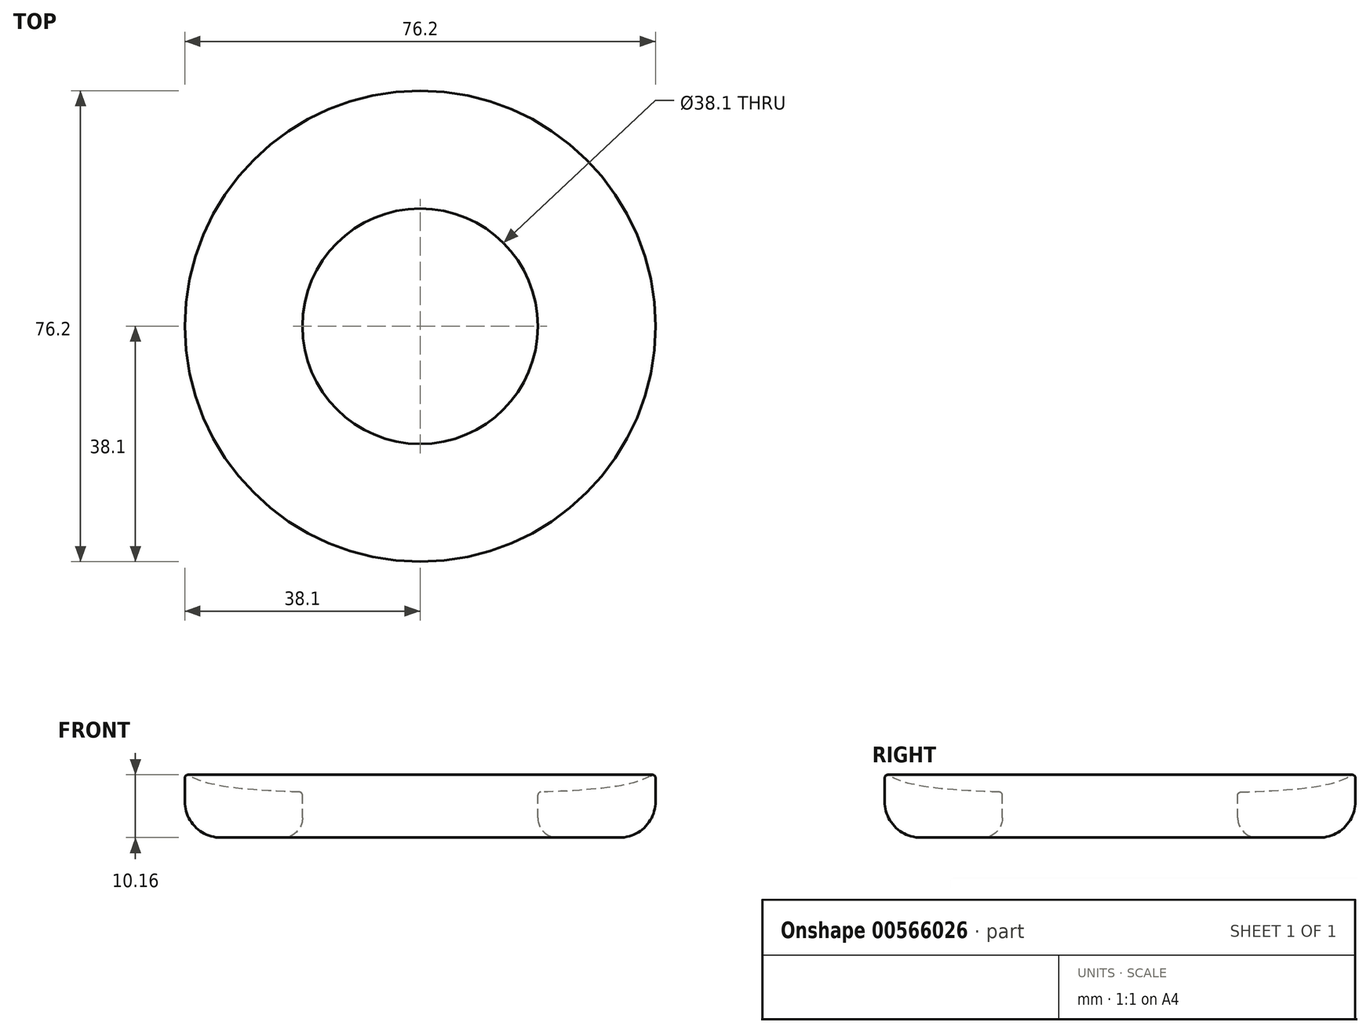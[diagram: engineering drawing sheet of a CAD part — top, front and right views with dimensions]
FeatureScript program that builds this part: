
annotation { "Feature Type Name" : "Feature", "Feature Type Description" : "" }
export const myFeature = defineFeature(function(context is Context, id is Id, definition is map)
    precondition{}
    {
        {
            var Q0;
            Q0=qCreatedBy(makeId("Front.planeOp"),FACE);
            var sketch = newSketch(context, id + "F0", { "sketchPlane" : qUnion([Q0])});
            skLineSegment(sketch, "E0.bottom", {"start": v(22.23, 0) * mm, "end": v(32.26, 0) * mm});
            skLineSegment(sketch, "E0.left", {"start": v(19.05, 3.17) * mm, "end": v(19.05, 6.86) * mm});
            skLineSegment(sketch, "E0.right", {"start": v(38.1, 5.84) * mm, "end": v(38.1, 9.65) * mm});
            skFitSpline(sketch, "E1", {"points": [v(38.1, 11) * mm, v(0, 6.84) * mm], "startDerivative": vector(-5.9, -12.6) * mm, "endDerivative": vector(-52.1, -2.11) * mm});
            skPoint(sketch, "E2.end.orphan", {"position": v(0, 11) * mm});
            skLineSegment(sketch, "E3", {"start": v(0, 11) * mm, "end": v(0, 0) * mm, "construction": true});
            skPoint(sketch, "E4.visualSharp", {"position": v(38.1, 0) * mm});
            skArc(sketch, "E4.filletArc", {"start": v(32.26, 0) * mm, "mid": v(36.39, 1.71) * mm, "end": v(38.1, 5.84) * mm});
            skPoint(sketch, "E5.visualSharp", {"position": v(19.05, 0) * mm});
            skArc(sketch, "E5.filletArc", {"start": v(19.05, 3.17) * mm, "mid": v(19.98, 0.93) * mm, "end": v(22.23, 0) * mm});
            skPoint(sketch, "E6.visualSharp", {"position": v(19.05, 7.35) * mm});
            skArc(sketch, "E6.filletArc", {"start": v(19.54, 7.37) * mm, "mid": v(19.2, 7.21) * mm, "end": v(19.05, 6.86) * mm});
            skArc(sketch, "E7.filletArc", {"start": v(38.1, 9.65) * mm, "mid": v(37.82, 10.1) * mm, "end": v(37.29, 10.06) * mm});
            skSolve(sketch);
        }
        {
            var Q0;
            Q0=makeQuery(id+"F0.imprint","IMPRINT",FACE,{"disambiguationData":[TD([[makeQuery(id+"F0.imprint","IMPRINT",EDGE,{"derivedFrom":sQuery(id+"F0.wireOp",EDGE,"E0.bottom")}),1.0]])]});
            var Q1;
            Q1=sQuery(id+"F0.wireOp",EDGE,"E3");
            revolve(context, id + "F1", {"entities" : qUnion([Q0]), "axis" : qUnion([Q1]), "revolveType" : RevolveType.FULL});
        }
    });
